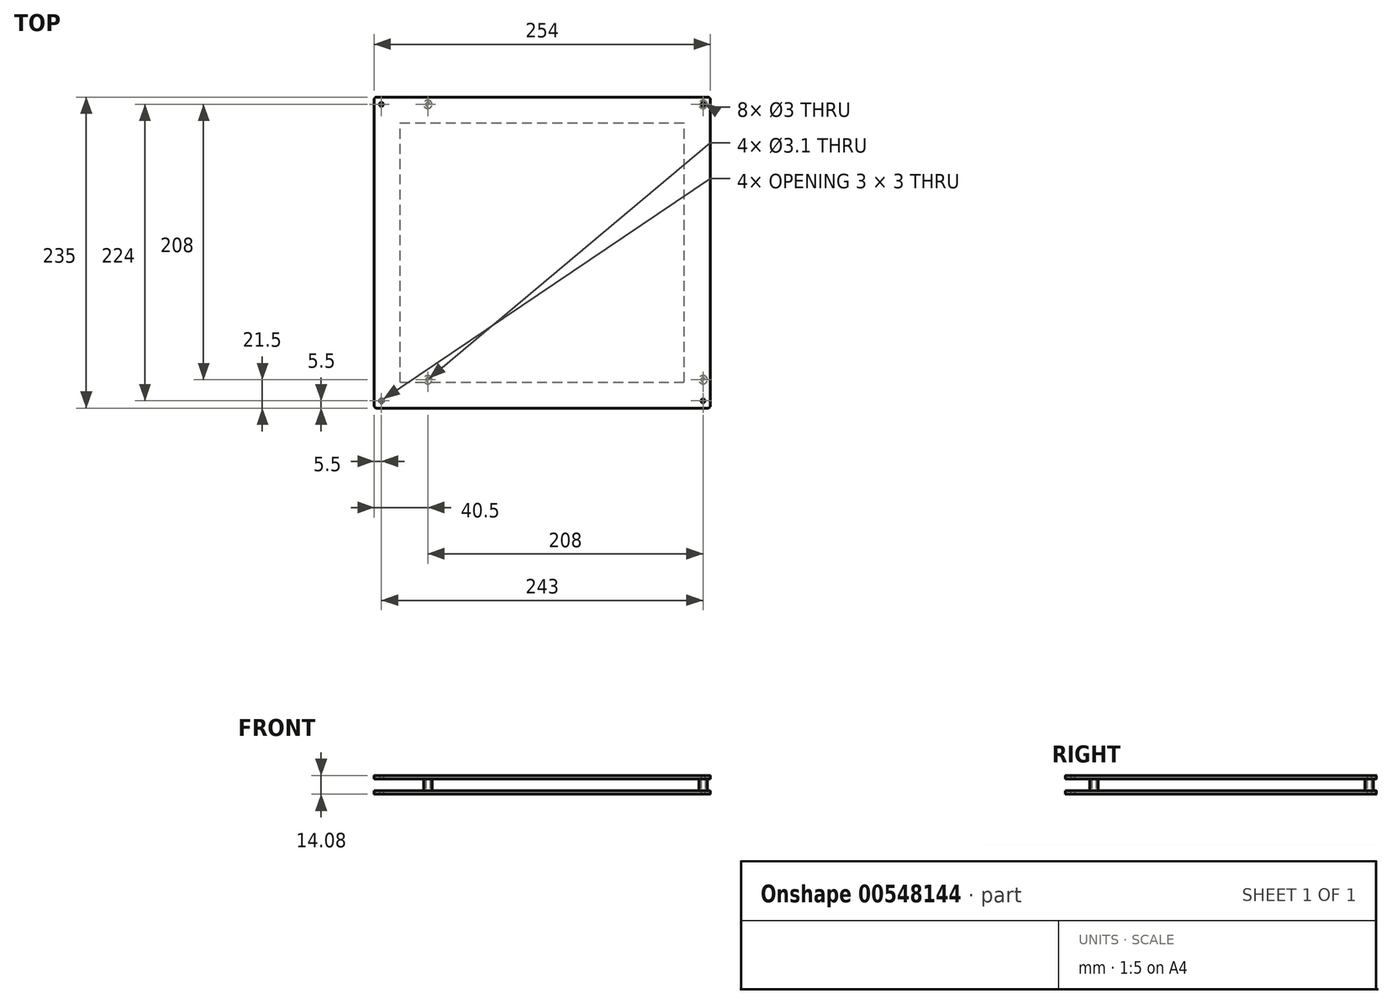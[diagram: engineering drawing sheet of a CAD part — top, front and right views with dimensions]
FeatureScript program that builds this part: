
annotation { "Feature Type Name" : "Feature", "Feature Type Description" : "" }
export const myFeature = defineFeature(function(context is Context, id is Id, definition is map)
    precondition{}
    {
        {
            var Q0;
            Q0=qCreatedBy(makeId("Top.planeOp"),FACE);
            var sketch = newSketch(context, id + "F0", { "sketchPlane" : qUnion([Q0])});
            skLineSegment(sketch, "E0.bottom", {"start": v(0, 0) * mm, "end": v(-254, 0) * mm});
            skLineSegment(sketch, "E0.top", {"start": v(0, -235) * mm, "end": v(-254, -235) * mm});
            skLineSegment(sketch, "E0.left", {"start": v(0, 0) * mm, "end": v(0, -235) * mm});
            skLineSegment(sketch, "E0.right", {"start": v(-254, 0) * mm, "end": v(-254, -235) * mm});
            skSolve(sketch);
        }
        {
            var Q0;
            Q0=makeQuery(id+"F0.imprint","IMPRINT",FACE,{"disambiguationData":[TD([[makeQuery(id+"F0.imprint","IMPRINT",EDGE,{"derivedFrom":sQuery(id+"F0.wireOp",EDGE,"E0.bottom")}),1.0]])]});
            var sketch = newSketch(context, id + "F1", { "sketchPlane" : qUnion([Q0])});
            skPoint(sketch, "E1", {"position": v(-5.5, -229.5) * mm});
            skPoint(sketch, "E2", {"position": v(-248.5, -229.5) * mm});
            skPoint(sketch, "E3", {"position": v(-248.5, -5.5) * mm});
            skPoint(sketch, "E4", {"position": v(-5.5, -5.5) * mm});
            skSolve(sketch);
        }
        {
            var Q0;
            Q0=makeQuery(id+"F0.imprint","IMPRINT",FACE,{"disambiguationData":[TD([[makeQuery(id+"F0.imprint","IMPRINT",EDGE,{"derivedFrom":sQuery(id+"F0.wireOp",EDGE,"E0.bottom")}),1.0]])]});
            extrude(context, id + "F2", {"entities" : qUnion([Q0]), "depth" : 2.54 * mm, "offsetDistance" : 25 * mm});
        }
        {
            var Q0;
            Q0=sQuery(id+"F1.wireOp",VERTEX,"E4");
            var Q1;
            Q1=sQuery(id+"F1.wireOp",VERTEX,"E1");
            var Q2;
            Q2=sQuery(id+"F1.wireOp",VERTEX,"E2");
            var Q3;
            Q3=sQuery(id+"F1.wireOp",VERTEX,"E3");
            var Q4;
            Q4=makeQuery(id+"F2.opExtrude","SWEPT_BODY",BODY,{"disambiguationData":[OSD([sQuery(id+"F0.wireOp",EDGE,"E0.bottom"),sQuery(id+"F0.wireOp",EDGE,"E0.top"),sQuery(id+"F0.wireOp",EDGE,"E0.left"),sQuery(id+"F0.wireOp",EDGE,"E0.right")])]});
            hole(context, id + "F3", {"style" : HoleStyle.SIMPLE, "endStyle" : HoleEndStyle.THROUGH, "oppositeDirection" : true, "holeDiameter" : 3 * mm, "isTappedThrough" : true, "tappedDepth" : 12 * mm, "tapClearance" : 3, "locations" : qUnion([Q0, Q1, Q2, Q3]), "scope" : qUnion([Q4])});
        }
        {
            var Q0;
            Q0=makeQuery(id+"F2.opExtrude","SWEPT_EDGE",EDGE,{"disambiguationData":[OSD([sQuery(id+"F0.wireOp",EDGE,"E0.top"),sQuery(id+"F0.wireOp",EDGE,"E0.right")])]});
            fillet(context, id + "F4", {"entities" : qUnion([Q0]), "radius" : 2 * mm, "tangentPropagation" : true, "allowEdgeOverflow" : false});
        }
        {
            var Q0;
            Q0=makeQuery(id+"F2.opExtrude","SWEPT_EDGE",EDGE,{"disambiguationData":[OSD([sQuery(id+"F0.wireOp",EDGE,"E0.bottom"),sQuery(id+"F0.wireOp",EDGE,"E0.right")])]});
            var Q1;
            Q1=makeQuery(id+"F2.opExtrude","SWEPT_EDGE",EDGE,{"disambiguationData":[OSD([sQuery(id+"F0.wireOp",EDGE,"E0.top"),sQuery(id+"F0.wireOp",EDGE,"E0.left")])]});
            fillet(context, id + "F5", {"entities" : qUnion([Q0, Q1]), "radius" : 2 * mm, "tangentPropagation" : true, "allowEdgeOverflow" : false});
        }
        {
            var Q0;
            Q0=makeQuery(id+"F2.opExtrude","SWEPT_EDGE",EDGE,{"disambiguationData":[OSD([sQuery(id+"F0.wireOp",EDGE,"E0.bottom"),sQuery(id+"F0.wireOp",EDGE,"E0.left")])]});
            fillet(context, id + "F6", {"entities" : qUnion([Q0]), "radius" : 2 * mm, "tangentPropagation" : true, "allowEdgeOverflow" : false});
        }
        {
            var Q0;
            Q0=makeQuery(id+"F2.opExtrude","CAP_EDGE",EDGE,{"disambiguationData":[OSD([sQuery(id+"F0.wireOp",EDGE,"E0.top")])],"isStart":false});
            fillet(context, id + "F7", {"entities" : qUnion([Q0]), "radius" : .1 * mm, "tangentPropagation" : true, "allowEdgeOverflow" : false});
        }
        {
            var Q0;
            Q0=makeQuery(id+"F2.opExtrude","CAP_EDGE",EDGE,{"disambiguationData":[OSD([sQuery(id+"F0.wireOp",EDGE,"E0.right")])],"isStart":true});
            fillet(context, id + "F8", {"entities" : qUnion([Q0]), "radius" : .1 * mm, "tangentPropagation" : true, "allowEdgeOverflow" : false});
        }
        {
            var Q0;
            Q0=makeQuery(id+"F2.opExtrude","SWEPT_BODY",BODY,{"disambiguationData":[OSD([sQuery(id+"F0.wireOp",EDGE,"E0.bottom"),sQuery(id+"F0.wireOp",EDGE,"E0.top"),sQuery(id+"F0.wireOp",EDGE,"E0.left"),sQuery(id+"F0.wireOp",EDGE,"E0.right")])]});
            transform(context, id + "F9", {"entities" : qUnion([Q0]), "transformType" : TransformType.TRANSLATION_3D, "dx" : 0 * mm, "dy" : 0 * mm, "dz" : 9 * mm, "makeCopy" : true});
        }
        {
            var Q0;
            Q0=qCreatedBy(makeId("Top.planeOp"),FACE);
            var sketch = newSketch(context, id + "F10", { "sketchPlane" : qUnion([Q0])});
            skCircle(sketch, "E5", {"center": v(0, 0) * mm, "radius": 3.17 * mm});
            skCircle(sketch, "E6", {"center": v(0, 0) * mm, "radius": 1.55 * mm});
            skSolve(sketch);
        }
        {
            var Q0;
            Q0=makeQuery(id+"F10.imprint","IMPRINT",FACE,{"disambiguationData":[TD([[makeQuery(id+"F10.imprint","IMPRINT",EDGE,{"derivedFrom":sQuery(id+"F10.wireOp",EDGE,"E5")}),1.0]])]});
            extrude(context, id + "F11", {"entities" : qUnion([Q0]), "depth" : 9 * mm, "offsetDistance" : 25 * mm});
        }
        {
            var Q0;
            Q0=makeQuery(id+"F2.opExtrude","SWEPT_BODY",BODY,{"disambiguationData":[OSD([sQuery(id+"F0.wireOp",EDGE,"E0.bottom"),sQuery(id+"F0.wireOp",EDGE,"E0.top"),sQuery(id+"F0.wireOp",EDGE,"E0.left"),sQuery(id+"F0.wireOp",EDGE,"E0.right")])]});
            transform(context, id + "F12", {"entities" : qUnion([Q0]), "transformType" : TransformType.TRANSLATION_3D, "dx" : 0 * mm, "dy" : 0 * mm, "dz" : -2.54 * mm, "makeCopy" : false});
        }
        {
            var Q0;
            Q0=makeQuery(id+"F11.opExtrude","SWEPT_BODY",BODY,{"disambiguationData":[OSD([sQuery(id+"F10.wireOp",EDGE,"E5"),sQuery(id+"F10.wireOp",EDGE,"E6")])]});
            transform(context, id + "F13", {"entities" : qUnion([Q0]), "transformType" : TransformType.TRANSLATION_3D, "dx" : -5.5 * mm, "dy" : -5.5 * mm, "dz" : 0 * mm, "makeCopy" : false});
        }
        {
            var Q0;
            Q0=makeQuery(id+"F11.opExtrude","SWEPT_BODY",BODY,{"disambiguationData":[OSD([sQuery(id+"F10.wireOp",EDGE,"E5"),sQuery(id+"F10.wireOp",EDGE,"E6")])]});
            transform(context, id + "F14", {"entities" : qUnion([Q0]), "transformType" : TransformType.TRANSLATION_3D, "dx" : 0 * mm, "dy" : -208 * mm, "dz" : 0 * mm, "makeCopy" : true});
        }
        {
            var Q0;
            Q0=makeQuery(id+"F14.opPattern","COPY",BODY,{"derivedFrom":makeQuery(id+"F11.opExtrude","SWEPT_BODY",BODY,{"disambiguationData":[OSD([sQuery(id+"F10.wireOp",EDGE,"E5"),sQuery(id+"F10.wireOp",EDGE,"E6")])]}),"instanceName":"1"});
            transform(context, id + "F15", {"entities" : qUnion([Q0]), "transformType" : TransformType.TRANSLATION_3D, "dx" : -208 * mm, "dy" : 0 * mm, "dz" : 0 * mm, "makeCopy" : true});
        }
        {
            var Q0;
            Q0=makeQuery(id+"F15.opPattern","COPY",BODY,{"derivedFrom":makeQuery(id+"F14.opPattern","COPY",BODY,{"derivedFrom":makeQuery(id+"F11.opExtrude","SWEPT_BODY",BODY,{"disambiguationData":[OSD([sQuery(id+"F10.wireOp",EDGE,"E5"),sQuery(id+"F10.wireOp",EDGE,"E6")])]}),"instanceName":"1"}),"instanceName":"1"});
            transform(context, id + "F16", {"entities" : qUnion([Q0]), "transformType" : TransformType.TRANSLATION_3D, "dx" : 0 * mm, "dy" : 208 * mm, "dz" : 0 * mm, "makeCopy" : true});
        }
        {
            var Q0;
            Q0=makeQuery(id+"F2.opExtrude","CAP_FACE",FACE,{"disambiguationData":[OSD([sQuery(id+"F0.wireOp",EDGE,"E0.bottom"),sQuery(id+"F0.wireOp",EDGE,"E0.top"),sQuery(id+"F0.wireOp",EDGE,"E0.left"),sQuery(id+"F0.wireOp",EDGE,"E0.right")])],"isStart":true});
            var sketch = newSketch(context, id + "F17", { "sketchPlane" : qUnion([Q0])});
            skLineSegment(sketch, "E7.bottom", {"start": v(-234.4, 215.4) * mm, "end": v(-19.6, 215.4) * mm, "construction": true});
            skLineSegment(sketch, "E7.top", {"start": v(-234.4, 19.6) * mm, "end": v(-19.6, 19.6) * mm, "construction": true});
            skLineSegment(sketch, "E7.left", {"start": v(-234.4, 215.4) * mm, "end": v(-234.4, 19.6) * mm, "construction": true});
            skLineSegment(sketch, "E7.right", {"start": v(-19.6, 215.4) * mm, "end": v(-19.6, 19.6) * mm, "construction": true});
            skLineSegment(sketch, "E8.bottom", {"start": v(-234.4, 215.4) * mm, "end": v(-19.6, 215.4) * mm});
            skLineSegment(sketch, "E8.top", {"start": v(-234.4, 19.6) * mm, "end": v(-19.6, 19.6) * mm});
            skLineSegment(sketch, "E8.left", {"start": v(-234.4, 215.4) * mm, "end": v(-234.4, 19.6) * mm});
            skLineSegment(sketch, "E8.right", {"start": v(-19.6, 215.4) * mm, "end": v(-19.6, 19.6) * mm});
            skSolve(sketch);
        }
        {
            var Q0;
            Q0=makeQuery(id+"F17.imprint","IMPRINT",FACE,{"disambiguationData":[TD([[makeQuery(id+"F17.imprint","IMPRINT",EDGE,{"derivedFrom":sQuery(id+"F17.wireOp",EDGE,"E8.bottom")}),-1.0]])]});
            extrude(context, id + "F18", {"entities" : qUnion([Q0]), "operationType" : NewBodyOperationType.REMOVE, "oppositeDirection" : true, "depth" : .5 * mm, "offsetDistance" : 25 * mm});
        }
    });
